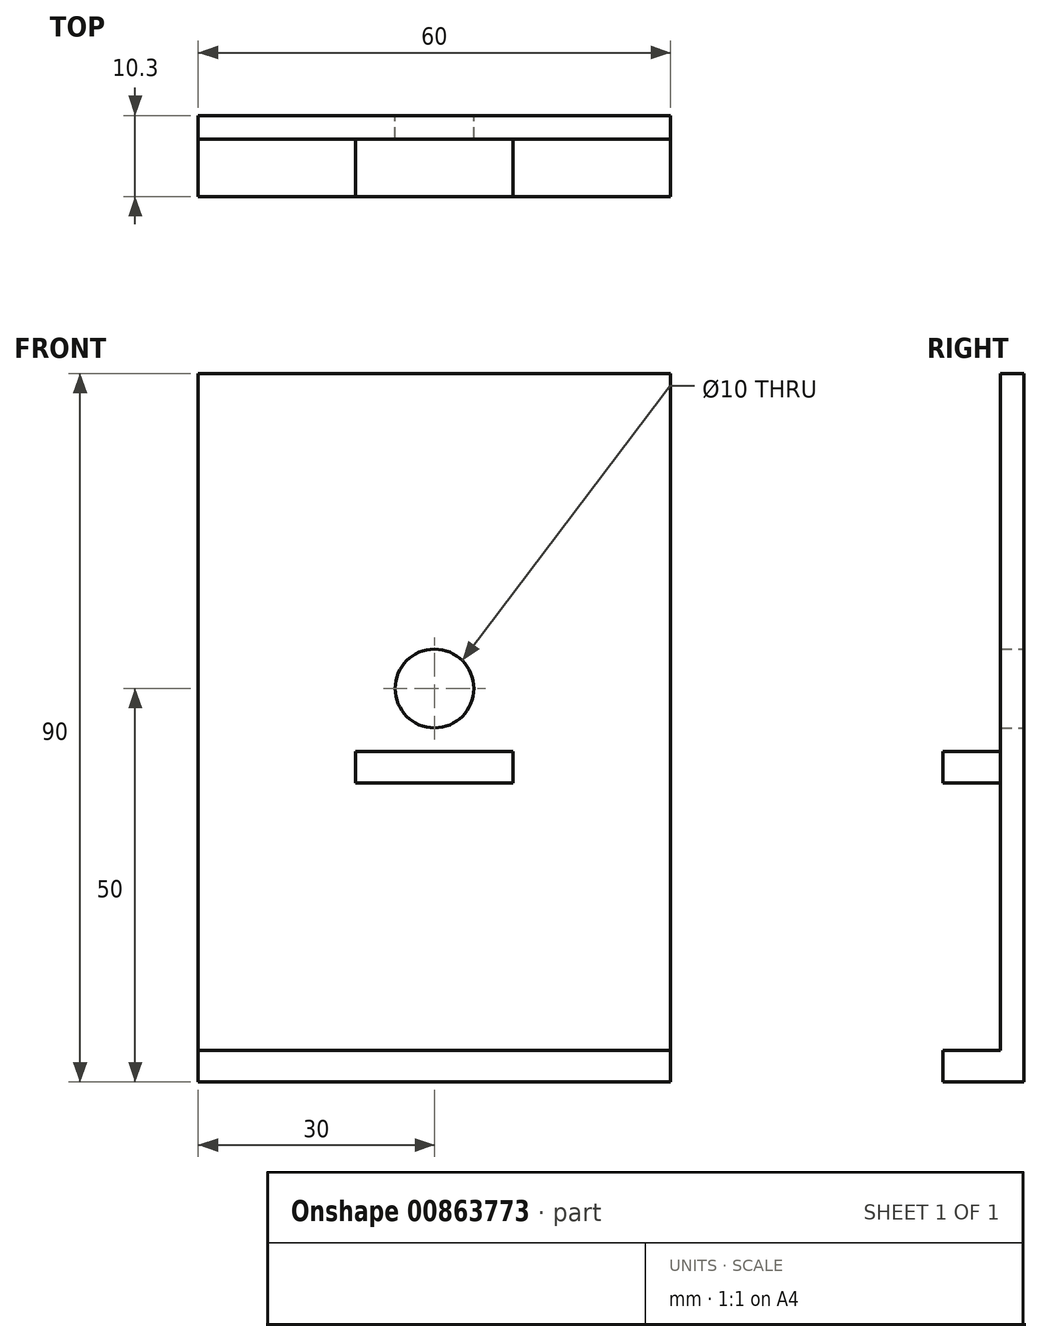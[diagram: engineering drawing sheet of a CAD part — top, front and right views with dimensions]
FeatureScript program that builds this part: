
annotation { "Feature Type Name" : "Feature", "Feature Type Description" : "" }
export const myFeature = defineFeature(function(context is Context, id is Id, definition is map)
    precondition{}
    {
        {
            var Q0;
            Q0=qCreatedBy(makeId("Front.planeOp"),FACE);
            var sketch = newSketch(context, id + "F0", { "sketchPlane" : qUnion([Q0])});
            skLineSegment(sketch, "E0.bottom", {"start": v(-30, 40) * mm, "end": v(30, 40) * mm});
            skLineSegment(sketch, "E0.top", {"start": v(-30, -50) * mm, "end": v(30, -50) * mm});
            skLineSegment(sketch, "E0.left", {"start": v(-30, 40) * mm, "end": v(-30, -50) * mm});
            skLineSegment(sketch, "E0.right", {"start": v(30, 40) * mm, "end": v(30, -50) * mm});
            skPoint(sketch, "E1", {"position": v(-30, 0) * mm});
            skPoint(sketch, "E2", {"position": v(0, 40) * mm});
            skSolve(sketch);
        }
        {
            var Q0;
            Q0=makeQuery(id+"F0.imprint","IMPRINT",FACE,{"disambiguationData":[TD([[makeQuery(id+"F0.imprint","IMPRINT",EDGE,{"derivedFrom":sQuery(id+"F0.wireOp",EDGE,"E0.bottom")}),-1.0]])]});
            var sketch = newSketch(context, id + "F1", { "sketchPlane" : qUnion([Q0])});
            skCircle(sketch, "E3", {"center": v(0, 0) * mm, "radius": 5 * mm});
            skSolve(sketch);
        }
        {
            var Q0;
            Q0=qSketchRegion(id+"F0",true);
            extrude(context, id + "F2", {"entities" : qUnion([Q0]), "depth" : 3 * mm, "offsetDistance" : 25.4 * mm});
        }
        {
            var Q0;
            Q0=qSketchRegion(id+"F1",true);
            extrude(context, id + "F3", {"entities" : qUnion([Q0]), "operationType" : NewBodyOperationType.REMOVE, "depth" : 25.4 * mm, "offsetDistance" : 25.4 * mm});
        }
        {
            var Q0;
            Q0=makeQuery(id+"F2.opExtrude","SWEPT_FACE",FACE,{"disambiguationData":[OSD([sQuery(id+"F0.wireOp",EDGE,"E0.top")])]});
            var sketch = newSketch(context, id + "F4", { "sketchPlane" : qUnion([Q0])});
            skLineSegment(sketch, "E4.bottom", {"start": v(-30, 0) * mm, "end": v(30, 0) * mm});
            skLineSegment(sketch, "E4.top", {"start": v(-30, 10.3) * mm, "end": v(30, 10.3) * mm});
            skLineSegment(sketch, "E4.left", {"start": v(-30, 0) * mm, "end": v(-30, 10.3) * mm});
            skLineSegment(sketch, "E4.right", {"start": v(30, 0) * mm, "end": v(30, 10.3) * mm});
            skSolve(sketch);
        }
        {
            var Q0;
            Q0=qSketchRegion(id+"F4",true);
            extrude(context, id + "F5", {"entities" : qUnion([Q0]), "operationType" : NewBodyOperationType.ADD, "oppositeDirection" : true, "depth" : 4 * mm, "offsetDistance" : 25.4 * mm});
        }
        {
            var Q0;
            Q0=qCreatedBy(makeId("Front.planeOp"),FACE);
            var sketch = newSketch(context, id + "F6", { "sketchPlane" : qUnion([Q0])});
            skLineSegment(sketch, "E5.bottom", {"start": v(-10, -8) * mm, "end": v(10, -8) * mm});
            skLineSegment(sketch, "E5.top", {"start": v(-10, -12) * mm, "end": v(10, -12) * mm});
            skLineSegment(sketch, "E5.left", {"start": v(-10, -8) * mm, "end": v(-10, -12) * mm});
            skLineSegment(sketch, "E5.right", {"start": v(10, -8) * mm, "end": v(10, -12) * mm});
            skPoint(sketch, "E6", {"position": v(0, -8) * mm});
            skPoint(sketch, "E7", {"position": v(-10, -10) * mm});
            skSolve(sketch);
        }
        {
            var Q0;
            Q0 = qSketchRegion(id + "F6", true);
            extrude(context, id + "F7", {"entities" : qUnion([Q0]), "operationType" : NewBodyOperationType.ADD, "depth" : 10.3 * mm, "offsetDistance" : 25.4 * mm});
        }
    });
